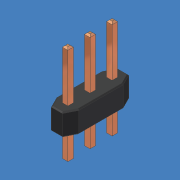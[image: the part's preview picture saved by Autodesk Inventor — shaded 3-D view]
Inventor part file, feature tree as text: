
AUTODESK INVENTOR PART (.ipt)
format: ipt  version: 2014 SP1 (Build 180222100, 222)  size: 203,776 bytes
history: native  units: mm (DEFAULTED — no unit token found)
features: chamfer x6, extrude x2, sketch x2, plane x1
ambient origin geometry x8: Origin, YZ Plane, XZ Plane, XY Plane, X Axis, Y Axis, Z Axis, Center Point
bodies: Solid1 (feature_tree)
feature tree (11):
  extrude  "Extrusion1"  Depth=7.62mm
  chamfer  "Chamfer1"  Distance=2.54mm
  chamfer  "Chamfer2"  Distance=0.9525mm
  chamfer  "Chamfer3"  Distance=2.54mm
  chamfer  "Chamfer4"  Distance=0.635mm
  plane  "Work Plane1"
  sketch  "Sketch2"  dims[d5=0.635mm d6=2.54mm d7=0.9525mm d8=2.54mm d9=0.0mm d10=1.27mm d11=0.635mm d12=1.27mm d13=0.635mm d14=1.27mm d15=0.635mm d16=1.27mm d17=0.635mm d18=3.175mm d19=11.43mm d20=0.0mm d21=0.1778mm d22=0.635mm d23=0.127mm d24=0.635mm d25=2.54mm d26=45.0deg d27=45.0deg d28=45.0deg d29=45.0deg d30=45.0deg d31=45.0deg]
  extrude  "Extrusion2"  Depth=0.635mm
  chamfer  "Chamfer5"  Distance=0.635mm
  chamfer  "Chamfer6"  Distance=0.635mm
  sketch  "Sketch1"  dims[d3=2.54mm d4=7.62mm]
